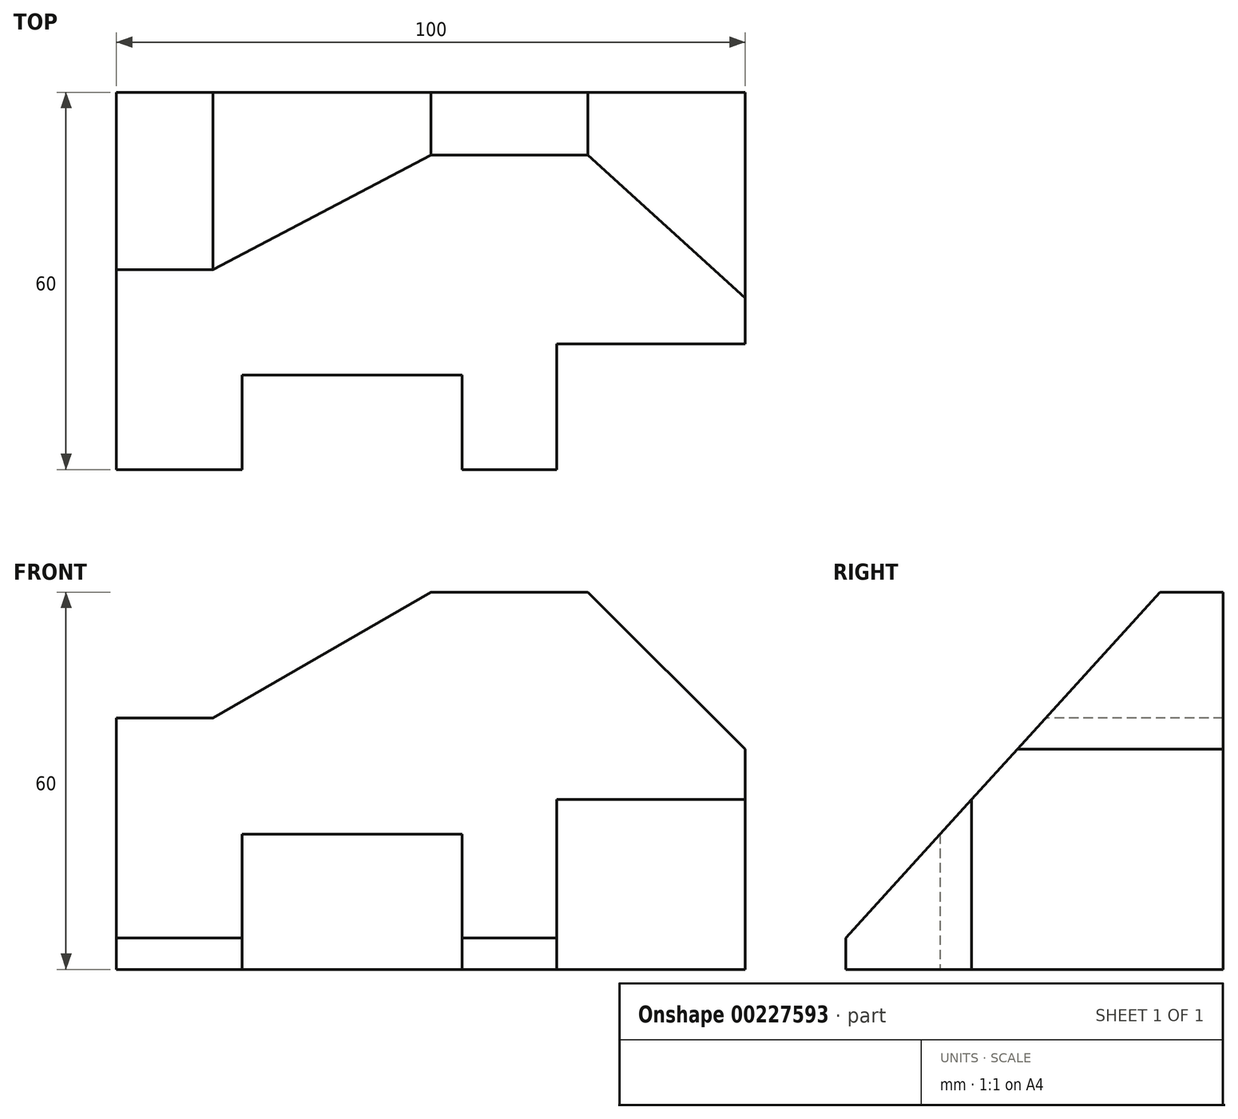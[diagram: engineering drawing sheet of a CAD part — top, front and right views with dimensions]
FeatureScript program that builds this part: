
annotation { "Feature Type Name" : "Feature", "Feature Type Description" : "" }
export const myFeature = defineFeature(function(context is Context, id is Id, definition is map)
    precondition{}
    {
        {
            var Q0;
            Q0=qCreatedBy(makeId("Top.planeOp"),FACE);
            var sketch = newSketch(context, id + "F0", { "sketchPlane" : qUnion([Q0])});
            skLineSegment(sketch, "E0", {"start": v(0, 0) * mm, "end": v(0, 60) * mm});
            skLineSegment(sketch, "E1", {"start": v(0, 60) * mm, "end": v(100, 60) * mm});
            skLineSegment(sketch, "E2", {"start": v(100, 60) * mm, "end": v(100, 20) * mm});
            skLineSegment(sketch, "E3", {"start": v(100, 20) * mm, "end": v(70, 20) * mm});
            skLineSegment(sketch, "E4", {"start": v(70, 20) * mm, "end": v(70, 0) * mm});
            skLineSegment(sketch, "E5", {"start": v(70, 0) * mm, "end": v(55, 0) * mm});
            skLineSegment(sketch, "E6", {"start": v(55, 0) * mm, "end": v(55, 15) * mm});
            skLineSegment(sketch, "E7", {"start": v(55, 15) * mm, "end": v(20, 15) * mm});
            skLineSegment(sketch, "E8", {"start": v(20, 15) * mm, "end": v(20, 0) * mm});
            skLineSegment(sketch, "E9", {"start": v(20, 0) * mm, "end": v(0, 0) * mm});
            skSolve(sketch);
        }
        {
            var Q0;
            Q0 = qSketchRegion(id + "F0", true);
            extrude(context, id + "F1", {"entities" : qUnion([Q0]), "depth" : 60 * mm});
        }
        {
            var Q0;
            Q0=qCreatedBy(makeId("Front.planeOp"),FACE);
            var sketch = newSketch(context, id + "F2", { "sketchPlane" : qUnion([Q0])});
            skPoint(sketch, "E10.0", {"position": v(70, 60) * mm});
            skLineSegment(sketch, "E11", {"start": v(75, 60) * mm, "end": v(100, 35) * mm});
            skLineSegment(sketch, "E12", {"start": v(75, 60) * mm, "end": v(100, 60) * mm});
            skLineSegment(sketch, "E13", {"start": v(100, 60) * mm, "end": v(100, 35) * mm});
            skLineSegment(sketch, "E14.0", {"start": v(0, 60) * mm, "end": v(0, 0) * mm, "construction": true});
            skLineSegment(sketch, "E15.0", {"start": v(20, 60) * mm, "end": v(0, 60) * mm, "construction": true});
            skLineSegment(sketch, "E16.0", {"start": v(55, 60) * mm, "end": v(20, 60) * mm, "construction": true});
            skLineSegment(sketch, "E17.0", {"start": v(20, 60) * mm, "end": v(20, 0) * mm, "construction": true});
            skLineSegment(sketch, "E18", {"start": v(0, 40) * mm, "end": v(15.36, 40) * mm});
            skLineSegment(sketch, "E19", {"start": v(15.36, 40) * mm, "end": v(50, 60) * mm});
            skLineSegment(sketch, "E20", {"start": v(50, 60) * mm, "end": v(0, 60) * mm});
            skLineSegment(sketch, "E21", {"start": v(0, 60) * mm, "end": v(0, 40) * mm});
            skLineSegment(sketch, "E22.0", {"start": v(100, 60) * mm, "end": v(70, 60) * mm, "construction": true});
            skLineSegment(sketch, "E23.0", {"start": v(100, 60) * mm, "end": v(100, 0) * mm, "construction": true});
            skSolve(sketch);
        }
        {
            var Q0;
            Q0 = qSketchRegion(id + "F2", true);
            extrude(context, id + "F3", {"entities" : qUnion([Q0]), "operationType" : NewBodyOperationType.REMOVE, "endBound" : BoundingType.THROUGH_ALL, "oppositeDirection" : true, "depth" : 25 * mm});
        }
        {
            var Q0;
            Q0=qCreatedBy(makeId("Right.planeOp"),FACE);
            var sketch = newSketch(context, id + "F4", { "sketchPlane" : qUnion([Q0])});
            skLineSegment(sketch, "E24.0", {"start": v(60, 60) * mm, "end": v(20, 60) * mm, "construction": true});
            skLineSegment(sketch, "E25.0", {"start": v(0, 60) * mm, "end": v(0, 0) * mm, "construction": true});
            skLineSegment(sketch, "E26.0", {"start": v(20, 60) * mm, "end": v(0, 60) * mm, "construction": true});
            skLineSegment(sketch, "E27", {"start": v(0, 5) * mm, "end": v(50, 60) * mm});
            skLineSegment(sketch, "E28", {"start": v(50, 60) * mm, "end": v(0, 60) * mm});
            skLineSegment(sketch, "E29", {"start": v(0, 5) * mm, "end": v(0, 60) * mm});
            skSolve(sketch);
        }
        {
            var Q0;
            Q0=makeQuery(id+"F4.imprint","IMPRINT",FACE,{"disambiguationData":[TD([[makeQuery(id+"F4.imprint","IMPRINT",EDGE,{"derivedFrom":sQuery(id+"F4.wireOp",EDGE,"E27")}),1.0]])]});
            extrude(context, id + "F5", {"entities" : qUnion([Q0]), "operationType" : NewBodyOperationType.REMOVE, "endBound" : BoundingType.THROUGH_ALL, "depth" : 25 * mm});
        }
    });
